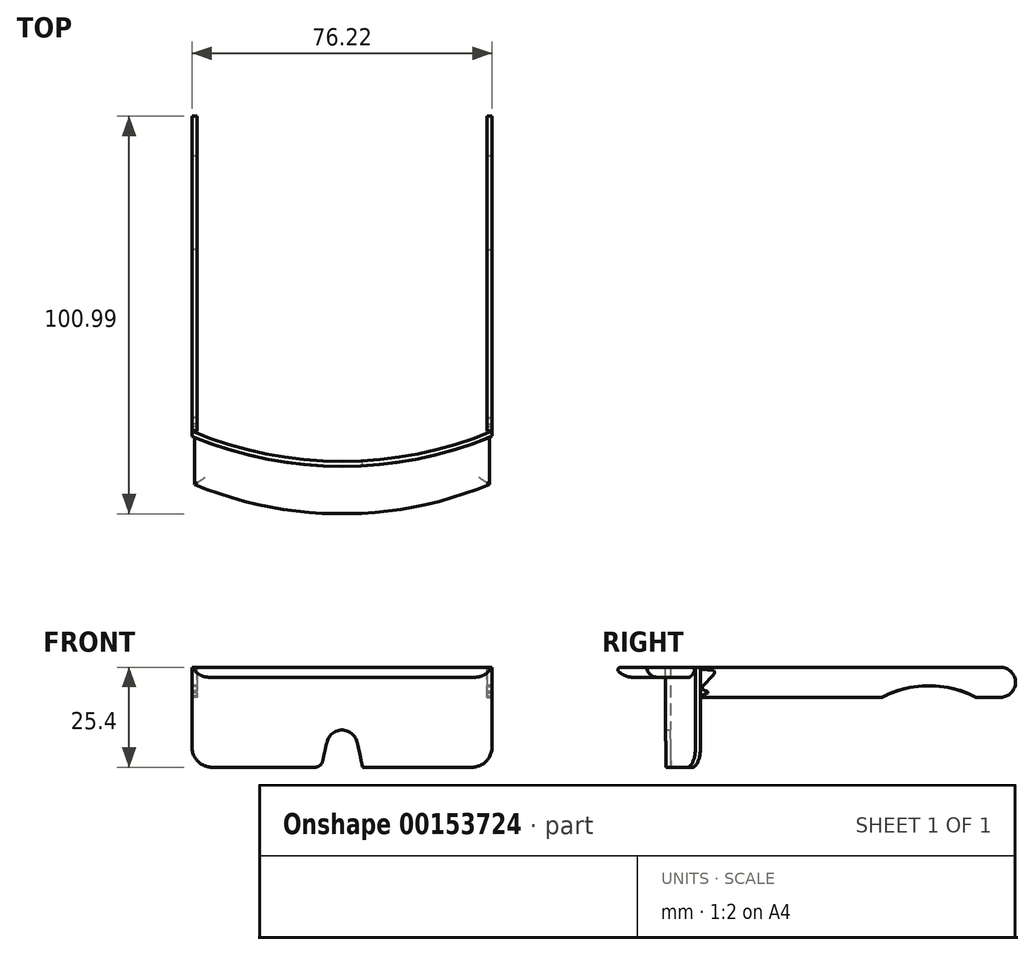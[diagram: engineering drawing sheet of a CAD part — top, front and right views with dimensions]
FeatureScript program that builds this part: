
annotation { "Feature Type Name" : "Feature", "Feature Type Description" : "" }
export const myFeature = defineFeature(function(context is Context, id is Id, definition is map)
    precondition{}
    {
        {
            var Q0;
            Q0=qCreatedBy(makeId("Top.planeOp"),FACE);
            var sketch = newSketch(context, id + "F0", { "sketchPlane" : qUnion([Q0])});
            skArc(sketch, "E0", {"start": v(-38.1, 0) * mm, "mid": v(0, -7.63) * mm, "end": v(38.1, 0) * mm});
            skLineSegment(sketch, "E1", {"start": v(-38.1, 0) * mm, "end": v(-38.1, -1.27) * mm});
            skLineSegment(sketch, "E2", {"start": v(38.1, 0) * mm, "end": v(38.1, -1.27) * mm});
            skArc(sketch, "E3", {"start": v(-38.1, -1.27) * mm, "mid": v(0, -8.9) * mm, "end": v(38.1, -1.27) * mm});
            skSolve(sketch);
        }
        {
            var Q0;
            Q0 = qSketchRegion(id + "F0", true);
            extrude(context, id + "F1", {"entities" : qUnion([Q0]), "depth" : 25.4 * mm});
        }
        {
            var Q0;
            Q0=qCreatedBy(makeId("Front.planeOp"),FACE);
            var sketch = newSketch(context, id + "F2", { "sketchPlane" : qUnion([Q0])});
            skLineSegment(sketch, "E4", {"start": v(0, 0) * mm, "end": v(-5.26, 0) * mm});
            skLineSegment(sketch, "E5", {"start": v(-5.26, 0) * mm, "end": v(-3.86, 6.35) * mm});
            skLineSegment(sketch, "E6.MirrorCS", {"start": v(0, 0) * mm, "end": v(5.26, 0) * mm});
            skLineSegment(sketch, "E7.MirrorCS", {"start": v(5.26, 0) * mm, "end": v(3.86, 6.35) * mm});
            skArc(sketch, "E8", {"start": v(3.86, 6.35) * mm, "mid": v(0, 9.45) * mm, "end": v(-3.86, 6.35) * mm});
            skSolve(sketch);
        }
        {
            var Q0;
            Q0 = qSketchRegion(id + "F2", true);
            extrude(context, id + "F3", {"entities" : qUnion([Q0]), "operationType" : NewBodyOperationType.REMOVE, "depth" : 25.4 * mm});
        }
        {
            var Q0;
            Q0=makeQuery(id+"F1.opExtrude","SWEPT_FACE",FACE,{"disambiguationData":[OSD([sQuery(id+"F0.wireOp",EDGE,"E2")])]});
            var sketch = newSketch(context, id + "F4", { "sketchPlane" : qUnion([Q0])});
            skLineSegment(sketch, "E9", {"start": v(0, 25.4) * mm, "end": v(76.2, 25.4) * mm});
            skLineSegment(sketch, "E10", {"start": v(0, 17.77) * mm, "end": v(76.2, 17.77) * mm});
            skArc(sketch, "E11", {"start": v(76.2, 17.77) * mm, "mid": v(80.02, 21.58) * mm, "end": v(76.2, 25.4) * mm});
            skLineSegment(sketch, "E12", {"start": v(3.37, 23.64) * mm, "end": v(0.5, 20.48) * mm});
            skArc(sketch, "E13", {"start": v(3.37, 23.64) * mm, "mid": v(3.55, 24.1) * mm, "end": v(3.37, 24.57) * mm});
            skArc(sketch, "E14", {"start": v(0.5, 20.48) * mm, "mid": v(0.63, 19.79) * mm, "end": v(1.24, 19.44) * mm});
            skArc(sketch, "E15", {"start": v(1.88, 18.89) * mm, "mid": v(1.67, 19.3) * mm, "end": v(1.24, 19.44) * mm});
            skLineSegment(sketch, "E16", {"start": v(3.37, 24.57) * mm, "end": v(0, 24.91) * mm});
            skLineSegment(sketch, "E17", {"start": v(1.88, 18.89) * mm, "end": v(0, 18.17) * mm});
            skLineSegment(sketch, "E18", {"start": v(0, 24.91) * mm, "end": v(0, 25.4) * mm});
            skLineSegment(sketch, "E19", {"start": v(0, 18.17) * mm, "end": v(0, 17.77) * mm});
            skSolve(sketch);
        }
        {
            var Q0;
            Q0 = qSketchRegion(id + "F4", true);
            extrude(context, id + "F5", {"entities" : qUnion([Q0]), "oppositeDirection" : true, "depth" : 1.27 * mm});
        }
        {
            var Q0;
            Q0=makeQuery(id+"F5.opExtrude","SWEPT_BODY",BODY,{"disambiguationData":[OSD([sQuery(id+"F4.wireOp",EDGE,"E9"),sQuery(id+"F4.wireOp",EDGE,"E10"),sQuery(id+"F4.wireOp",EDGE,"E11"),sQuery(id+"F4.wireOp",EDGE,"E12"),sQuery(id+"F4.wireOp",EDGE,"E13"),sQuery(id+"F4.wireOp",EDGE,"E14"),sQuery(id+"F4.wireOp",EDGE,"E15"),sQuery(id+"F4.wireOp",EDGE,"E16"),sQuery(id+"F4.wireOp",EDGE,"E17"),sQuery(id+"F4.wireOp",EDGE,"E18"),sQuery(id+"F4.wireOp",EDGE,"E19")])]});
            var Q1;
            Q1=qCreatedBy(makeId("Right.planeOp"),FACE);
            mirror(context, id + "F6", {"entities" : qUnion([Q0]), "mirrorPlane" : qUnion([Q1])});
        }
        {
            var Q0;
            Q0=makeQuery(id+"F1.opExtrude","CAP_EDGE",EDGE,{"disambiguationData":[OSD([sQuery(id+"F0.wireOp",EDGE,"E1")])],"isStart":true});
            var Q1;
            Q1=makeQuery(id+"F3.boolean.opBoolean","COPY",EDGE,{"derivedFrom":makeQuery(id+"F3.opExtrude","SWEPT_EDGE",EDGE,{"disambiguationData":[OSD([sQuery(id+"F2.wireOp",EDGE,"yaCku8Z0-dCSW-Ddr9-cSzq-9QpyhOpIMAlw"),sQuery(id+"F2.wireOp",EDGE,"ix1K2hcp-CE5P-eKfI-KgJq-lqh3GIPjbydG")])]})});
            var Q2;
            Q2=makeQuery(id+"F1.opExtrude","CAP_EDGE",EDGE,{"disambiguationData":[OSD([sQuery(id+"F0.wireOp",EDGE,"E2")])],"isStart":true});
            var Q3;
            Q3=makeQuery(id+"F3.boolean.opBoolean","COPY",EDGE,{"derivedFrom":makeQuery(id+"F3.opExtrude","SWEPT_EDGE",EDGE,{"disambiguationData":[OSD([sQuery(id+"F2.wireOp",EDGE,"f7bb0fe2-e2ea-484a-8e12-0a164c678d330.MirrorCS"),sQuery(id+"F2.wireOp",EDGE,"fb1f2ff5-479f-494f-aab6-4164c3ce34150.MirrorCS")])]})});
            fillet(context, id + "F7", {"entities" : qUnion([Q0, Q1, Q2, Q3]), "radius" : 5.08 * mm, "tangentPropagation" : true, "allowEdgeOverflow" : false});
        }
        {
            var Q0;
            Q0=makeQuery(id+"F1.opExtrude","CAP_FACE",FACE,{"disambiguationData":[OSD([sQuery(id+"F0.wireOp",EDGE,"E0"),sQuery(id+"F0.wireOp",EDGE,"E1"),sQuery(id+"F0.wireOp",EDGE,"E2"),sQuery(id+"F0.wireOp",EDGE,"E3")])],"isStart":false});
            var sketch = newSketch(context, id + "F8", { "sketchPlane" : qUnion([Q0])});
            skLineSegment(sketch, "E20", {"start": v(-38.1, -1.27) * mm, "end": v(-38.1, -13.97) * mm});
            skLineSegment(sketch, "E21", {"start": v(0, -8.9) * mm, "end": v(0, -21.62) * mm});
            skPoint(sketch, "E21.startSnap0", {"position": v(0, -8.9) * mm});
            skLineSegment(sketch, "E22.MirrorCS", {"start": v(38.1, -1.27) * mm, "end": v(38.1, -13.97) * mm});
            skArc(sketch, "E23", {"start": v(-38.1, -13.97) * mm, "mid": v(0, -21.62) * mm, "end": v(38.1, -13.97) * mm});
            skSolve(sketch);
        }
        {
            var Q0;
            {var subQ0=sQuery(id+"F8.wireOp",EDGE,"E20");Q0=makeQuery(id+"F8.imprint","IMPRINT",FACE,{"disambiguationData":[TD([[makeQuery(id+"F8.imprint","IMPRINT",EDGE,{"derivedFrom":subQ0}),1.0]])]});}
            var Q1;
            {var subQ0=sQuery(id+"F8.wireOp",EDGE,"E21");Q1=makeQuery(id+"F8.imprint","IMPRINT",FACE,{"disambiguationData":[TD([[makeQuery(id+"F8.imprint","IMPRINT",EDGE,{"derivedFrom":subQ0}),1.0]])]});}
            extrude(context, id + "F9", {"entities" : qUnion([Q0, Q1]), "oppositeDirection" : true, "depth" : 2.54 * mm});
        }
        {
            var Q0;
            Q0=makeQuery(id+"F9.opExtrude","CAP_EDGE",EDGE,{"disambiguationData":[OSD([sQuery(id+"F8.wireOp",EDGE,"E22.MirrorCS")])],"isStart":false});
            var Q1;
            Q1=makeQuery(id+"F9.opExtrude","CAP_EDGE",EDGE,{"disambiguationData":[OSD([sQuery(id+"F8.wireOp",EDGE,"E23")])],"isStart":false});
            var Q2;
            Q2=makeQuery(id+"F9.opExtrude","CAP_EDGE",EDGE,{"disambiguationData":[OSD([sQuery(id+"F8.wireOp",EDGE,"E20")])],"isStart":false});
            fillet(context, id + "F10", {"entities" : qUnion([Q0, Q1, Q2]), "radius" : 5.08 * mm, "tangentPropagation" : true, "allowEdgeOverflow" : false});
        }
        {
            var Q0;
            {var subQ0=sQuery(id+"F8.wireOp",EDGE,"E23");Q0=makeQuery(id+"F10.opFillet","BLEND_EDGE",EDGE,{"blendedFrom":[makeQuery(id+"F9.opExtrude","CAP_EDGE",EDGE,{"disambiguationData":[OSD([subQ0])],"isStart":false}),makeQuery(id+"F9.opExtrude","CAP_FACE",FACE,{"disambiguationData":[OSD([sQuery(id+"F0.wireOp",EDGE,"E3"),sQuery(id+"F8.wireOp",EDGE,"E20"),sQuery(id+"F8.wireOp",EDGE,"E22.MirrorCS"),subQ0])],"isStart":true})],"blendedInto":[makeQuery(id+"F9.opExtrude","CAP_FACE",FACE,{"disambiguationData":[OSD([sQuery(id+"F0.wireOp",EDGE,"E3"),sQuery(id+"F8.wireOp",EDGE,"E20"),sQuery(id+"F8.wireOp",EDGE,"E22.MirrorCS"),subQ0])],"isStart":true})]});}
            var Q1;
            {var subQ0=sQuery(id+"F8.wireOp",EDGE,"E22.MirrorCS");Q1=makeQuery(id+"F10.opFillet","BLEND_EDGE",EDGE,{"blendedFrom":[makeQuery(id+"F9.opExtrude","CAP_EDGE",EDGE,{"disambiguationData":[OSD([subQ0])],"isStart":false}),makeQuery(id+"F9.opExtrude","CAP_FACE",FACE,{"disambiguationData":[OSD([sQuery(id+"F0.wireOp",EDGE,"E3"),sQuery(id+"F8.wireOp",EDGE,"E20"),subQ0,sQuery(id+"F8.wireOp",EDGE,"E23")])],"isStart":true})],"blendedInto":[makeQuery(id+"F9.opExtrude","CAP_FACE",FACE,{"disambiguationData":[OSD([sQuery(id+"F0.wireOp",EDGE,"E3"),sQuery(id+"F8.wireOp",EDGE,"E20"),subQ0,sQuery(id+"F8.wireOp",EDGE,"E23")])],"isStart":true})]});}
            var Q2;
            {var subQ0=sQuery(id+"F8.wireOp",EDGE,"E20");Q2=makeQuery(id+"F10.opFillet","BLEND_EDGE",EDGE,{"blendedFrom":[makeQuery(id+"F9.opExtrude","CAP_EDGE",EDGE,{"disambiguationData":[OSD([subQ0])],"isStart":false}),makeQuery(id+"F9.opExtrude","CAP_FACE",FACE,{"disambiguationData":[OSD([sQuery(id+"F0.wireOp",EDGE,"E3"),subQ0,sQuery(id+"F8.wireOp",EDGE,"E22.MirrorCS"),sQuery(id+"F8.wireOp",EDGE,"E23")])],"isStart":true})],"blendedInto":[makeQuery(id+"F9.opExtrude","CAP_FACE",FACE,{"disambiguationData":[OSD([sQuery(id+"F0.wireOp",EDGE,"E3"),subQ0,sQuery(id+"F8.wireOp",EDGE,"E22.MirrorCS"),sQuery(id+"F8.wireOp",EDGE,"E23")])],"isStart":true})]});}
            fillet(context, id + "F11", {"entities" : qUnion([Q0, Q1, Q2]), "radius" : 0.64 * mm, "tangentPropagation" : true, "allowEdgeOverflow" : false});
        }
        {
            var Q0;
            Q0=makeQuery(id+"F6.opPattern","COPY",FACE,{"derivedFrom":makeQuery(id+"F5.opExtrude","CAP_FACE",FACE,{"disambiguationData":[OSD([sQuery(id+"F4.wireOp",EDGE,"E9"),sQuery(id+"F4.wireOp",EDGE,"E10"),sQuery(id+"F4.wireOp",EDGE,"E11"),sQuery(id+"F4.wireOp",EDGE,"E12"),sQuery(id+"F4.wireOp",EDGE,"E13"),sQuery(id+"F4.wireOp",EDGE,"E14"),sQuery(id+"F4.wireOp",EDGE,"E15"),sQuery(id+"F4.wireOp",EDGE,"E16"),sQuery(id+"F4.wireOp",EDGE,"E17"),sQuery(id+"F4.wireOp",EDGE,"E18"),sQuery(id+"F4.wireOp",EDGE,"E19")])],"isStart":true}),"instanceName":"1"});
            var sketch = newSketch(context, id + "F12", { "sketchPlane" : qUnion([Q0])});
            skArc(sketch, "E24", {"start": v(-46.14, 17.77) * mm, "mid": v(-58.04, 20.73) * mm, "end": v(-69.94, 17.77) * mm});
            skLineSegment(sketch, "E25", {"start": v(-69.94, 17.77) * mm, "end": v(-46.14, 17.77) * mm});
            skSolve(sketch);
        }
        {
            var Q0;
            Q0 = qSketchRegion(id + "F12", true);
            var Q1;
            Q1=makeQuery(id+"F5.opExtrude","CAP_FACE",FACE,{"disambiguationData":[OSD([sQuery(id+"F4.wireOp",EDGE,"E9"),sQuery(id+"F4.wireOp",EDGE,"E10"),sQuery(id+"F4.wireOp",EDGE,"E11"),sQuery(id+"F4.wireOp",EDGE,"E12"),sQuery(id+"F4.wireOp",EDGE,"E13"),sQuery(id+"F4.wireOp",EDGE,"E14"),sQuery(id+"F4.wireOp",EDGE,"E15"),sQuery(id+"F4.wireOp",EDGE,"E16"),sQuery(id+"F4.wireOp",EDGE,"E17"),sQuery(id+"F4.wireOp",EDGE,"E18"),sQuery(id+"F4.wireOp",EDGE,"E19")])],"isStart":true});
            extrude(context, id + "F13", {"entities" : qUnion([Q0]), "operationType" : NewBodyOperationType.REMOVE, "endBound" : BoundingType.UP_TO_SURFACE, "oppositeDirection" : true, "endBoundEntityFace" : qUnion([Q1]), "depth" : 25.4 * mm});
        }
        {
            var Q0;
            Q0=makeQuery(id+"F5.opExtrude","CAP_FACE",FACE,{"disambiguationData":[OSD([sQuery(id+"F4.wireOp",EDGE,"E9"),sQuery(id+"F4.wireOp",EDGE,"E10"),sQuery(id+"F4.wireOp",EDGE,"E11"),sQuery(id+"F4.wireOp",EDGE,"E12"),sQuery(id+"F4.wireOp",EDGE,"E13"),sQuery(id+"F4.wireOp",EDGE,"E14"),sQuery(id+"F4.wireOp",EDGE,"E15"),sQuery(id+"F4.wireOp",EDGE,"E16"),sQuery(id+"F4.wireOp",EDGE,"E17"),sQuery(id+"F4.wireOp",EDGE,"E18"),sQuery(id+"F4.wireOp",EDGE,"E19")])],"isStart":true});
            var sketch = newSketch(context, id + "F14", { "sketchPlane" : qUnion([Q0])});
            skArc(sketch, "E26", {"start": v(69.94, 17.77) * mm, "mid": v(58.04, 20.73) * mm, "end": v(46.14, 17.77) * mm});
            skLineSegment(sketch, "E27", {"start": v(46.14, 17.77) * mm, "end": v(69.94, 17.77) * mm});
            skSolve(sketch);
        }
        {
            var Q0;
            Q0 = qSketchRegion(id + "F14", true);
            extrude(context, id + "F15", {"entities" : qUnion([Q0]), "operationType" : NewBodyOperationType.REMOVE, "oppositeDirection" : true, "depth" : 25.4 * mm});
        }
        {
            var Q0;
            Q0=makeQuery(id+"F3.boolean.opBoolean","COPY",EDGE,{"derivedFrom":makeQuery(id+"F3.opExtrude","SWEPT_EDGE",EDGE,{"disambiguationData":[OSD([sQuery(id+"F2.wireOp",EDGE,"E4"),sQuery(id+"F2.wireOp",EDGE,"E5")])]})});
            var Q1;
            Q1=makeQuery(id+"F3.boolean.opBoolean","COPY",EDGE,{"derivedFrom":makeQuery(id+"F3.opExtrude","SWEPT_EDGE",EDGE,{"disambiguationData":[OSD([sQuery(id+"F2.wireOp",EDGE,"E6.MirrorCS"),sQuery(id+"F2.wireOp",EDGE,"E7.MirrorCS")])]})});
            fillet(context, id + "F16", {"entities" : qUnion([Q0, Q1]), "radius" : 2.02 * mm, "tangentPropagation" : true, "allowEdgeOverflow" : false});
        }
    });
